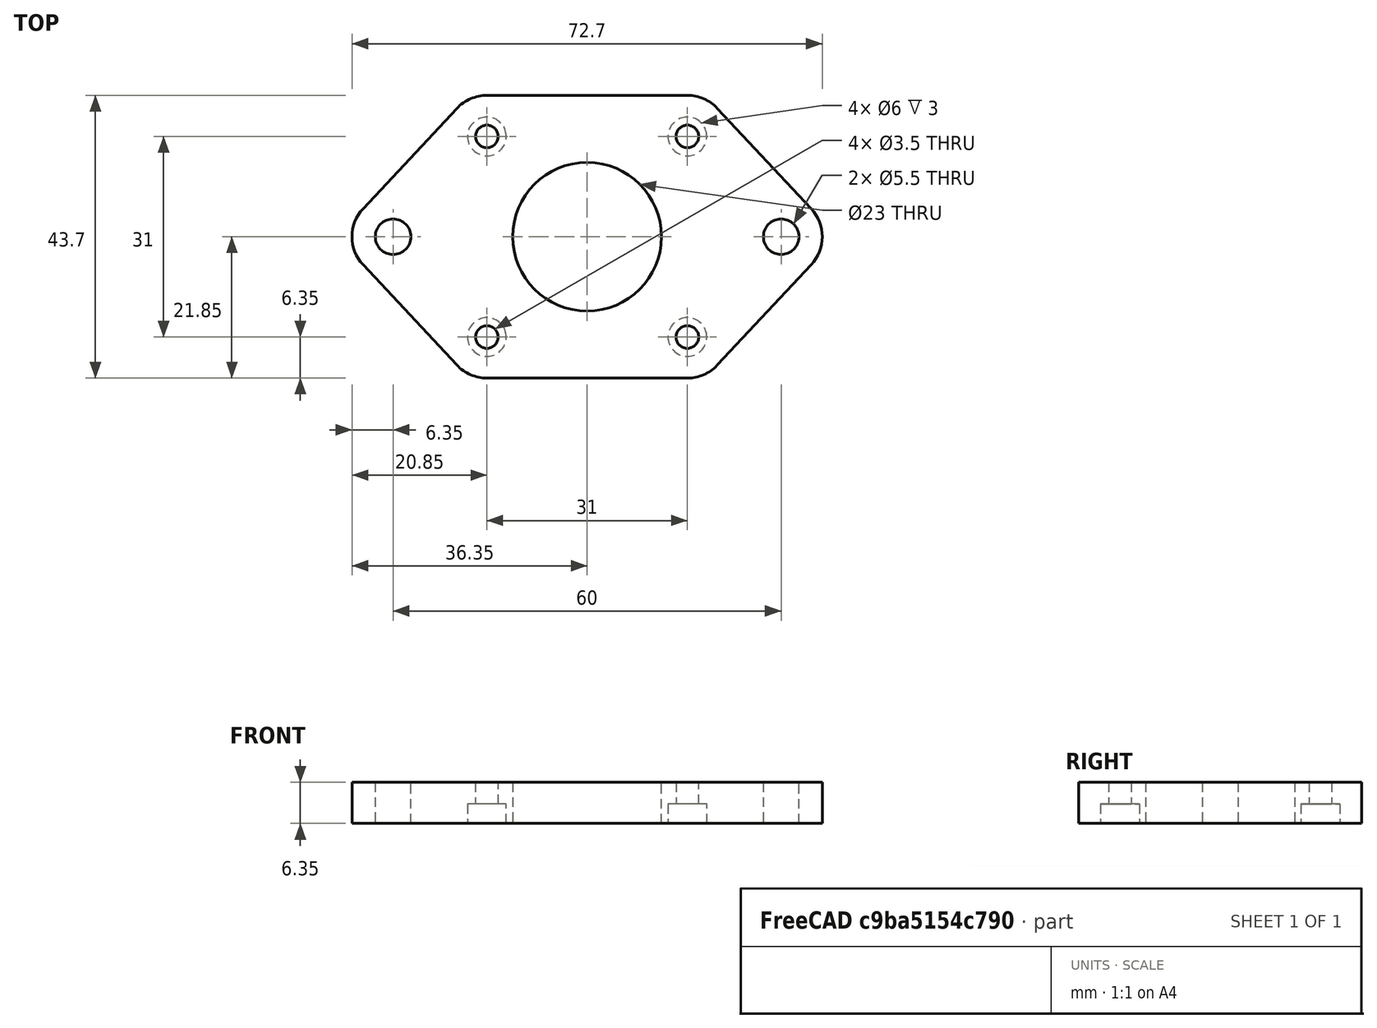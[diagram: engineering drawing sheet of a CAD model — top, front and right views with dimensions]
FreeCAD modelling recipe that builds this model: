
FCSTD DOCUMENT  (FreeCAD 0.19R23578 (Git))
Label: z_motor_adaptor_plate
License: All rights reserved
LicenseURL: http://en.wikipedia.org/wiki/All_rights_reserved
objects: TechDraw::DrawViewDimension×6, PartDesign::CoordinateSystem×4, Sketcher::SketchObject×2, TechDraw::DrawViewDimExtent×2, PartDesign::Pad×1, PartDesign::Pocket×1, PartDesign::Body×1, TechDraw::DrawSVGTemplate×1, TechDraw::DrawProjGroupItem×1, TechDraw::DrawProjGroup×1, TechDraw::DrawPage×1, App::Part×1
note: 11 computed .brp shape members not serialized (recipe doc carries the construction recipe); baked Part::Feature solids carry a one-line shape summary decoded from their .brp

FEATURE [Sketcher::SketchObject] Sketch093
  MapMode = 5
  Support = -> [XY_Plane105]
  expr: Constraints[43] = 60
  sketch-geometry (23):
    g0: LineSegment StartX=-34.6372 StartY=4.33805 StartZ=0 EndX=-20.1372 EndY=19.838 EndZ=0
    g1: LineSegment StartX=-15.5 StartY=21.85 StartZ=0 EndX=15.5 EndY=21.85 EndZ=0
    g2: LineSegment StartX=20.1372 StartY=19.838 StartZ=0 EndX=34.6372 EndY=4.33805 EndZ=0
    g3: LineSegment StartX=34.6372 StartY=-4.33805 StartZ=0 EndX=20.1372 EndY=-19.838 EndZ=0
    g4: LineSegment StartX=15.5 StartY=-21.85 StartZ=0 EndX=-15.5 EndY=-21.85 EndZ=0
    g5: LineSegment StartX=-20.1372 StartY=-19.838 StartZ=0 EndX=-34.6372 EndY=-4.33805 EndZ=0
    g6: ArcOfCircle CenterX=-30 CenterY=0 CenterZ=0 NormalX=0 NormalY=0 NormalZ=1 AngleXU=0 Radius=6.35 StartAngle=2.38952 EndAngle=3.89367
    g7: ArcOfCircle CenterX=-15.5 CenterY=15.5 CenterZ=0 NormalX=0 NormalY=0 NormalZ=1 AngleXU=0 Radius=6.35 StartAngle=1.5708 EndAngle=2.38952
    g8: ArcOfCircle CenterX=15.5 CenterY=15.5 CenterZ=0 NormalX=0 NormalY=0 NormalZ=1 AngleXU=0 Radius=6.35 StartAngle=0.752077 EndAngle=1.5708
    g9: ArcOfCircle CenterX=30 CenterY=0 CenterZ=0 NormalX=0 NormalY=0 NormalZ=1 AngleXU=0 Radius=6.35 StartAngle=5.53111 EndAngle=7.03526
    g10: ArcOfCircle CenterX=15.5 CenterY=-15.5 CenterZ=0 NormalX=0 NormalY=0 NormalZ=1 AngleXU=0 Radius=6.35 StartAngle=4.71239 EndAngle=5.53111
    g11: ArcOfCircle CenterX=-15.5 CenterY=-15.5 CenterZ=0 NormalX=0 NormalY=0 NormalZ=1 AngleXU=0 Radius=6.35 StartAngle=3.89367 EndAngle=4.71239
    g12: LineSegment StartX=-15.5 StartY=15.5 StartZ=0 EndX=15.5 EndY=15.5 EndZ=0
    g13: LineSegment StartX=15.5 StartY=15.5 StartZ=0 EndX=15.5 EndY=-15.5 EndZ=0
    g14: LineSegment StartX=15.5 StartY=-15.5 StartZ=0 EndX=-15.5 EndY=-15.5 EndZ=0
    g15: LineSegment StartX=-15.5 StartY=-15.5 StartZ=0 EndX=-15.5 EndY=15.5 EndZ=0
    g16: Circle CenterX=-15.5 CenterY=15.5 CenterZ=0 NormalX=0 NormalY=0 NormalZ=1 AngleXU=0 Radius=1.75
    g17: Circle CenterX=15.5 CenterY=15.5 CenterZ=0 NormalX=0 NormalY=0 NormalZ=1 AngleXU=0 Radius=1.75
    g18: Circle CenterX=15.5 CenterY=-15.5 CenterZ=0 NormalX=0 NormalY=0 NormalZ=1 AngleXU=0 Radius=1.75
    g19: Circle CenterX=-15.5 CenterY=-15.5 CenterZ=0 NormalX=0 NormalY=0 NormalZ=1 AngleXU=0 Radius=1.75
    g20: Circle CenterX=-30 CenterY=0 CenterZ=0 NormalX=0 NormalY=0 NormalZ=1 AngleXU=0 Radius=2.75
    g21: Circle CenterX=30 CenterY=0 CenterZ=0 NormalX=0 NormalY=0 NormalZ=1 AngleXU=0 Radius=2.75
    g22: Circle CenterX=0 CenterY=0 CenterZ=0 NormalX=0 NormalY=0 NormalZ=1 AngleXU=0 Radius=11.5
  constraints (49):
    c: Tangent(g0,g6) = 1.5708
    c: Tangent(g5,g6) = 1.5708
    c: Tangent(g0,g7) = 1.5708
    c: Tangent(g1,g7) = 1.5708
    c: Tangent(g1,g8) = 1.5708
    c: Tangent(g2,g8) = 1.5708
    c: Tangent(g2,g9) = 1.5708
    c: Tangent(g3,g9) = 1.5708
    c: Tangent(g3,g10) = 1.5708
    c: Tangent(g4,g10) = 1.5708
    c: Tangent(g4,g11) = 1.5708
    c: Tangent(g5,g11) = 1.5708
    c: Coincident(g12,g13)
    c: Coincident(g13,g14)
    c: Coincident(g14,g15)
    c: Coincident(g15,g12)
    c: Horizontal(g14)
    c: Vertical(g15)
    c: Coincident(g16,g12)
    c: Coincident(g17,g12)
    c: Coincident(g18,g13)
    c: Coincident(g19,g14)
    c: Equal(g16,g17)
    c: Equal(g17,g18)
    c: Equal(g18,g19)
    c: Diameter(g17) = 3.5
    c: Equal(g7,g6)
    c: Equal(g6,g11)
    c: Equal(g11,g10)
    c: Equal(g10,g8)
    c: Equal(g8,g9)
    c: Radius(g9) = 6.35
    c: Symmetric(g1,g4,g-1)
    c: Symmetric(g9,g6,g-2)
    c: Coincident(g20,g6)
    c: Coincident(g21,g9)
    c: PointOnObject(g6,g-1)
    c: Symmetric(g1,g1,g-2)
    c: Symmetric(g4,g4,g-2)
    c: Symmetric(g18,g17,g-1)
    c: Symmetric(g17,g16,g-2)
    c: Equal(g12,g13)
    c: DistanceX(g12,g12) = 31
    c: DistanceX(g6,g9) = 60
    c: Coincident(g8,g17)
    c: Coincident(g22,g-1)
    c: Diameter(g22) = 23
    c: Equal(g20,g21)
    c: Diameter(g21) = 5.5
FEATURE [PartDesign::Pad] Pad032  label="Pad033"
  Direction = (1,1,1)
  Length = 6.35
  Length2 = 100
  Profile = -> Sketch093
  Type = 0
FEATURE [Sketcher::SketchObject] Sketch094
  MapMode = 5
  Support = -> [XY_Plane105]
  sketch-geometry (8):
    g0: LineSegment StartX=-15.5 StartY=15.5 StartZ=0 EndX=15.5 EndY=15.5 EndZ=0
    g1: LineSegment StartX=15.5 StartY=15.5 StartZ=0 EndX=15.5 EndY=-15.5 EndZ=0
    g2: LineSegment StartX=15.5 StartY=-15.5 StartZ=0 EndX=-15.5 EndY=-15.5 EndZ=0
    g3: LineSegment StartX=-15.5 StartY=-15.5 StartZ=0 EndX=-15.5 EndY=15.5 EndZ=0
    g4: Circle CenterX=-15.5 CenterY=15.5 CenterZ=0 NormalX=0 NormalY=0 NormalZ=1 AngleXU=0 Radius=3
    g5: Circle CenterX=15.5 CenterY=15.5 CenterZ=0 NormalX=0 NormalY=0 NormalZ=1 AngleXU=0 Radius=3
    g6: Circle CenterX=15.5 CenterY=-15.5 CenterZ=0 NormalX=0 NormalY=0 NormalZ=1 AngleXU=0 Radius=3
    g7: Circle CenterX=-15.5 CenterY=-15.5 CenterZ=0 NormalX=0 NormalY=0 NormalZ=1 AngleXU=0 Radius=3
  constraints (18):
    c: Coincident(g0,g1)
    c: Coincident(g1,g2)
    c: Coincident(g2,g3)
    c: Coincident(g3,g0)
    c: Horizontal(g2)
    c: Vertical(g3)
    c: Coincident(g4,g0)
    c: Coincident(g5,g0)
    c: Coincident(g6,g1)
    c: Coincident(g7,g2)
    c: Equal(g5,g4)
    c: Equal(g4,g7)
    c: Equal(g7,g6)
    c: Diameter(g5) = 6
    c: Symmetric(g5,g6,g-1)
    c: Symmetric(g5,g4,g-2)
    c: DistanceX(g0,g0) = 31
    c: Equal(g3,g0)
FEATURE [PartDesign::Pocket] Pocket027
  BaseFeature = -> Pad032
  Length = 3
  Length2 = 100
  Profile = -> Sketch094
  Reversed = true
  Type = 0
FEATURE [PartDesign::Body] Body036  label="Body"
  Group = -> [Sketch093,Pad032,Sketch094,Pocket027]
  Origin = -> Origin105
  Tip = -> Pocket027
FEATURE [TechDraw::DrawSVGTemplate] Template010
  EditableTexts = Author=Alex Neufeld; DWG_num=2020-112; Date=11/07/2020; Revision=1; Scale=NTS; Subtitle=1 Req; Title=Z Axis Motor Bracket
  Height = 215.9
  Orientation = 1
  Width = 279.4
FEATURE [TechDraw::DrawProjGroupItem] ProjItem036  label="Front011"
  CoarseView = false
  Direction = (0,0,1)
  Focus = 100
  HardHidden = false
  IsoCount = 0
  IsoHidden = false
  IsoVisible = false
  LockPosition = true
  Perspective = false
  Rotation = 90
  RotationVector = (1,0,0)
  ScaleType = 2
  SeamHidden = false
  SeamVisible = true
  SmoothHidden = false
  SmoothVisible = true
  Source = -> [Body036]
  Type = 0
  X = 0
  XDirection = (1e-16,1,0)
  Y = 0
FEATURE [TechDraw::DrawProjGroup] ProjGroup011
  Anchor = -> ProjItem036
  AutoDistribute = true
  LockPosition = false
  ProjectionType = 0
  Rotation = 0
  ScaleType = 0
  Source = -> [Body036]
  Views = -> [ProjItem036]
  X = 139.7
  Y = 107.95
  spacingX = 15
  spacingY = 15
FEATURE [TechDraw::DrawViewDimExtent] DimExtent013
  Arbitrary = false
  ArbitraryTolerances = false
  CosmeticTags = b4d62288-45a0-4493-b462-dada78fb5f72 | ba20ee15-e9d9-4cfa-af9a-7a2251a67fee
  DirExtent = 0
  FormatSpec = %.3f
  FormatSpecOverTolerance = %+.2f
  FormatSpecUnderTolerance = %+.2f
  Inverted = false
  LockPosition = false
  MeasureType = 1
  OverTolerance = 0
  References2D = -> [ProjItem036]
  Rotation = 0
  ScaleType = 0
  Source = -> [ProjItem036]
  TheoreticalExact = false
  Type = 1
  UnderTolerance = 0
  X = 2.15719
  Y = 33.0755
FEATURE [TechDraw::DrawViewDimExtent] DimExtent014
  Arbitrary = false
  ArbitraryTolerances = false
  CosmeticTags = 38caeeea-741a-4d1c-8500-c1ebbf708ce5 | 3d63ee3c-2b32-485c-9a31-cd0c80d53145
  DirExtent = 1
  FormatSpec = %.3f
  FormatSpecOverTolerance = %+.2f
  FormatSpecUnderTolerance = %+.2f
  Inverted = false
  LockPosition = false
  MeasureType = 1
  OverTolerance = 0
  References2D = -> [ProjItem036]
  Rotation = 0
  ScaleType = 0
  Source = -> [ProjItem036]
  TheoreticalExact = false
  Type = 2
  UnderTolerance = 0
  X = 41.7766
  Y = -0.503435
FEATURE [TechDraw::DrawViewDimension] Dimension179
  Arbitrary = false
  ArbitraryTolerances = false
  FormatSpec = %.3f
  FormatSpecOverTolerance = %+.2f
  FormatSpecUnderTolerance = %+.2f
  Inverted = false
  LockPosition = false
  MeasureType = 1
  OverTolerance = 0
  References2D = -> [ProjItem036]
  Rotation = 0
  ScaleType = 0
  TheoreticalExact = false
  Type = 1
  UnderTolerance = 0
  X = -0.34372
  Y = -37.8094
FEATURE [TechDraw::DrawViewDimension] Dimension180
  Arbitrary = false
  ArbitraryTolerances = false
  FormatSpec = ⌀%.3f
  FormatSpecOverTolerance = %+.2f
  FormatSpecUnderTolerance = %+.2f
  Inverted = false
  LockPosition = false
  MeasureType = 1
  OverTolerance = 0
  References2D = -> [ProjItem036]
  Rotation = 0
  ScaleType = 0
  TheoreticalExact = false
  Type = 5
  UnderTolerance = 0
  X = -69.6032
  Y = 2.5779
FEATURE [TechDraw::DrawViewDimension] Dimension181
  Arbitrary = false
  ArbitraryTolerances = false
  FormatSpec = ⌀%.3f
  FormatSpecOverTolerance = %+.2f
  FormatSpecUnderTolerance = %+.2f
  Inverted = false
  LockPosition = false
  MeasureType = 1
  OverTolerance = 0
  References2D = -> [ProjItem036]
  Rotation = 0
  ScaleType = 0
  TheoreticalExact = false
  Type = 5
  UnderTolerance = 0
  X = -4.2965
  Y = 0.716083
FEATURE [TechDraw::DrawViewDimension] Dimension182
  Arbitrary = false
  ArbitraryTolerances = false
  FormatSpec = ⌀%.3f
  FormatSpecOverTolerance = %+.2f
  FormatSpecUnderTolerance = %+.2f
  Inverted = false
  LockPosition = false
  MeasureType = 1
  OverTolerance = 0
  References2D = -> [ProjItem036]
  Rotation = 0
  ScaleType = 0
  TheoreticalExact = false
  Type = 5
  UnderTolerance = 0
  X = 41.0745
  Y = 43.3087
FEATURE [TechDraw::DrawViewDimension] Dimension183
  Arbitrary = false
  ArbitraryTolerances = false
  FormatSpec = %.3f
  FormatSpecOverTolerance = %+.2f
  FormatSpecUnderTolerance = %+.2f
  Inverted = false
  LockPosition = false
  MeasureType = 1
  OverTolerance = 0
  References2D = -> [ProjItem036]
  Rotation = 0
  ScaleType = 0
  TheoreticalExact = false
  Type = 1
  UnderTolerance = 0
  X = -2.00503
  Y = -17.5364
FEATURE [TechDraw::DrawViewDimension] Dimension184
  Arbitrary = false
  ArbitraryTolerances = false
  FormatSpec = %.3f
  FormatSpecOverTolerance = %+.2f
  FormatSpecUnderTolerance = %+.2f
  Inverted = false
  LockPosition = false
  MeasureType = 1
  OverTolerance = 0
  References2D = -> [ProjItem036]
  Rotation = 0
  ScaleType = 0
  TheoreticalExact = false
  Type = 2
  UnderTolerance = 0
  X = -26.5951
  Y = 0.0656065
FEATURE [TechDraw::DrawPage] Page010  label="z_bracket_dwg"
  KeepUpdated = false
  NextBalloonIndex = 1
  ProjectionType = 0
  Template = -> Template010
  Views = -> [ProjGroup011,DimExtent013,DimExtent014,Dimension179,Dimension180,Dimension181,Dimension182,Dimension183,Dimension184]
FEATURE [PartDesign::CoordinateSystem] LCS_1
  AttacherType = Attacher::AttachEngine3D
  MapMode = 11
  Placement = pos=(0,0,0) rot=(0,0,1;1.5708rad)
  Support = -> [Pocket027]
FEATURE [PartDesign::CoordinateSystem] LCS_2
  AttacherType = Attacher::AttachEngine3D
  MapMode = 11
  Placement = pos=(0,0,6.35) rot=(0,0,1;1.5708rad)
  Support = -> [Pocket027]
FEATURE [PartDesign::CoordinateSystem] LCS_3
  AttacherType = Attacher::AttachEngine3D
  MapMode = 11
  Placement = pos=(-30,0,6.35) rot=(0,0,1;1.5708rad)
  Support = -> [Pocket027]
FEATURE [PartDesign::CoordinateSystem] LCS_4
  AttacherType = Attacher::AttachEngine3D
  MapMode = 11
  Placement = pos=(30,0,6.35) rot=(0,0,1;1.5708rad)
  Support = -> [Pocket027]
FEATURE [App::Part] Part  label="z_motor_adaptor_plate"
  Group = -> [Body036,LCS_1,LCS_2,LCS_3,LCS_4]
  Origin = -> Origin
